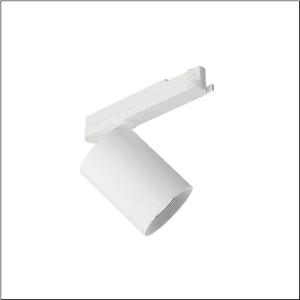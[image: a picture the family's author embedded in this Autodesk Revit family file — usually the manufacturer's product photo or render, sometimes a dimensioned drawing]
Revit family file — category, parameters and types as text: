
# Revit family: spot_21_51se13mbd5b
name_source: partatom
category: Lighting Fixtures
units: mm (PartAtom-declared; Revit-internal decimal feet)

## family parameters
Cut with Voids When Loaded = No
Host = Face
Light Source = No
Part Type = Normal
Room Calculation Point = No
Round Connector Dimension = Use Diameter
Shared = No

## types (1)
- --- (1 x LED, 5520 lm, 41.5 W, 4000K)
    Apparent Load = 42 VA
    CIE Flux Codes = 95 98 99 100 100
    Color Rendering = 90
    Color Temperature = 4000K
    Default Elevation = 1800 mm
    Description = Spot 21, directional spotlight, light control with lens, of PMMA, LED rated luminous flux: 5.300lm, light colour: 940, control gear: ECG Multilumen, with 3-phase adapter, mains connection: 220..240V, AC, 50/60Hz, of aluminium, traffic white (RAL 9016), length: 213mm, diameter: 105mm, protection rating (complete): IP20, insulation class (complete): insulation class I (protective earthing), certification: CE, impact resistance: IK02, permissible ambient temperature for indoor applications: -20..+40°C, packaging unit: 1 piece
    Height = 175 mm
    Lamp = 1 x LED
    Lamp Light Flux = 5520 lm
    Lamp Power = 41.5 W
    Lamp count = 1
    Length = 105 mm
    Luminous efficacy = 133 lm/W
    Manufacturer = Siteco
    ModVariant = No
    Model = 51SE13MBD5B
    Mounting Place = Ceiling
    Mounting Type = Pendant
    Number of Poles = 1
    OnlyDefault = Yes
    Power Factor = 1
    Product Name = Spot 21
    Product group = directional spotlight
    ProductGroupID = 905
    Protection Class = Protection class I
    Protection Degree = IP 20
    RLX_Detail_Level = 1
    RLX_Emergency_Light_Flux = 0 lm
    RLX_Emergency_Type = 0
    RLX_Emergency_Type_DB = No
    RlxData = <blob elided: 17613 chars, md5=7b32d03d>
    Socket = socket
    Standby Power = 0 W
    System Light Flux = 5520 lm
    System Power = 42 W
    Type Comments = factory setting: luminous flux: 100 % | (ON | ON | ON | ON) | 1050 mA
    Type Image = l_1003976.jpg
    URL = http://relux.com
    VarID = @adj_093649
    Voltage = 0 V
    Weight = 0.00 kg
    Width = 0 mm  [stored 0 ft]

note: [stored X ft] marks values corroborated as IEEE doubles in the binary element streams (Revit-internal decimal feet)

## geometry (parser evidence)
native form markers: Blend x4, Sweep x10
no freeform markers — native parametric forms only
